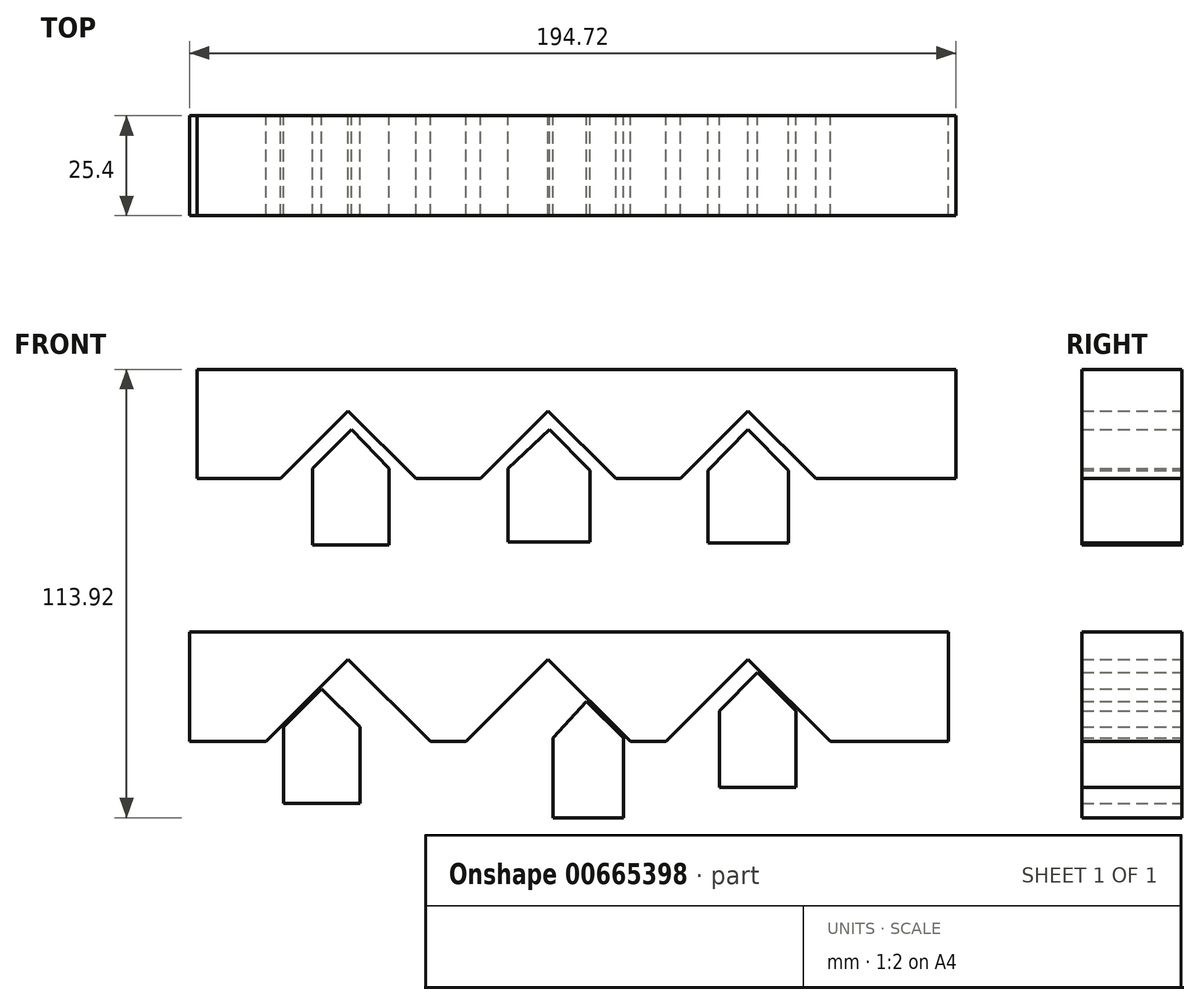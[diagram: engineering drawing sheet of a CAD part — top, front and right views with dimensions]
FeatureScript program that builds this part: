
annotation { "Feature Type Name" : "Feature", "Feature Type Description" : "" }
export const myFeature = defineFeature(function(context is Context, id is Id, definition is map)
    precondition{}
    {
        {
            var Q0;
            Q0=qCreatedBy(makeId("Front.planeOp"),FACE);
            var sketch = newSketch(context, id + "F0", { "sketchPlane" : qUnion([Q0])});
            skLineSegment(sketch, "E0", {"start": v(-96.29, 37.96) * mm, "end": v(96.47, 37.96) * mm});
            skLineSegment(sketch, "E1", {"start": v(96.47, 37.96) * mm, "end": v(96.47, 10.18) * mm});
            skLineSegment(sketch, "E2", {"start": v(96.47, 10.18) * mm, "end": v(60.84, 10.18) * mm});
            skLineSegment(sketch, "E3", {"start": v(60.84, 10.18) * mm, "end": v(43.68, 27.33) * mm});
            skLineSegment(sketch, "E4", {"start": v(43.68, 27.33) * mm, "end": v(26.53, 10.18) * mm});
            skLineSegment(sketch, "E5", {"start": v(26.53, 10.18) * mm, "end": v(10.04, 10.18) * mm});
            skLineSegment(sketch, "E6", {"start": v(-40.76, 10.18) * mm, "end": v(-57.92, 27.33) * mm});
            skLineSegment(sketch, "E7", {"start": v(-57.92, 27.33) * mm, "end": v(-75.07, 10.18) * mm});
            skLineSegment(sketch, "E8", {"start": v(-75.07, 10.18) * mm, "end": v(-96.29, 10.18) * mm});
            skLineSegment(sketch, "E9", {"start": v(-96.29, 10.18) * mm, "end": v(-96.29, 37.96) * mm});
            skLineSegment(sketch, "E10", {"start": v(-24.27, 10.18) * mm, "end": v(-7.12, 27.33) * mm});
            skLineSegment(sketch, "E11", {"start": v(-7.12, 27.33) * mm, "end": v(10.04, 10.18) * mm});
            skLineSegment(sketch, "E12.trimOffspring", {"start": v(-24.27, 10.18) * mm, "end": v(-40.76, 10.18) * mm});
            skLineSegment(sketch, "E13", {"start": v(-98.25, -28.81) * mm, "end": v(94.5, -28.81) * mm});
            skLineSegment(sketch, "E14", {"start": v(94.5, -28.81) * mm, "end": v(94.5, -56.6) * mm});
            skLineSegment(sketch, "E15", {"start": v(94.5, -56.6) * mm, "end": v(64.52, -56.6) * mm});
            skLineSegment(sketch, "E16", {"start": v(64.52, -56.6) * mm, "end": v(43.68, -35.77) * mm});
            skLineSegment(sketch, "E17", {"start": v(43.68, -35.77) * mm, "end": v(22.85, -56.6) * mm});
            skLineSegment(sketch, "E18", {"start": v(22.85, -56.6) * mm, "end": v(13.72, -56.6) * mm});
            skLineSegment(sketch, "E19", {"start": v(-37.08, -56.6) * mm, "end": v(-57.92, -35.77) * mm});
            skLineSegment(sketch, "E20", {"start": v(-57.92, -35.77) * mm, "end": v(-78.75, -56.6) * mm});
            skLineSegment(sketch, "E21", {"start": v(-78.75, -56.6) * mm, "end": v(-98.25, -56.6) * mm});
            skLineSegment(sketch, "E22", {"start": v(-98.25, -56.6) * mm, "end": v(-98.25, -28.81) * mm});
            skLineSegment(sketch, "E23", {"start": v(-27.95, -56.6) * mm, "end": v(-7.12, -35.77) * mm});
            skLineSegment(sketch, "E24", {"start": v(-7.12, -35.77) * mm, "end": v(13.72, -56.6) * mm});
            skLineSegment(sketch, "E25.trimOffspring", {"start": v(-27.95, -56.6) * mm, "end": v(-37.08, -56.6) * mm});
            skLineSegment(sketch, "E26", {"start": v(-57.1, 22.65) * mm, "end": v(-67.01, 12.74) * mm});
            skLineSegment(sketch, "E27", {"start": v(-47.57, 12.75) * mm, "end": v(-57.1, 22.65) * mm});
            skLineSegment(sketch, "E28", {"start": v(-6.74, 22.65) * mm, "end": v(-17.34, 12.75) * mm});
            skLineSegment(sketch, "E29", {"start": v(3.47, 12.24) * mm, "end": v(-6.74, 22.65) * mm});
            skLineSegment(sketch, "E30", {"start": v(43.64, 22.65) * mm, "end": v(33.42, 12.24) * mm});
            skLineSegment(sketch, "E31", {"start": v(53.86, 12.24) * mm, "end": v(43.64, 22.65) * mm});
            skLineSegment(sketch, "E32", {"start": v(-64.67, -43.22) * mm, "end": v(-74.39, -52.94) * mm});
            skLineSegment(sketch, "E33", {"start": v(-54.96, -52.94) * mm, "end": v(-64.67, -43.22) * mm});
            skLineSegment(sketch, "E34", {"start": v(2.65, -46.42) * mm, "end": v(-5.92, -55.74) * mm});
            skLineSegment(sketch, "E35", {"start": v(11.97, -55.74) * mm, "end": v(2.65, -46.42) * mm});
            skLineSegment(sketch, "E36", {"start": v(46.05, -39.08) * mm, "end": v(36.33, -48.8) * mm});
            skLineSegment(sketch, "E37", {"start": v(55.76, -48.8) * mm, "end": v(46.05, -39.08) * mm});
            skLineSegment(sketch, "E38", {"start": v(-67.01, 12.74) * mm, "end": v(-67.01, -6.7) * mm});
            skLineSegment(sketch, "E39", {"start": v(-67.01, -6.7) * mm, "end": v(-47.57, -6.7) * mm});
            skLineSegment(sketch, "E40", {"start": v(-47.57, -6.7) * mm, "end": v(-47.57, 12.75) * mm});
            skLineSegment(sketch, "E41", {"start": v(-17.34, 12.75) * mm, "end": v(-17.34, -5.87) * mm});
            skLineSegment(sketch, "E42", {"start": v(-17.34, -5.87) * mm, "end": v(3.47, -5.87) * mm});
            skLineSegment(sketch, "E43", {"start": v(3.47, -5.87) * mm, "end": v(3.47, 12.24) * mm});
            skLineSegment(sketch, "E44", {"start": v(33.42, 12.24) * mm, "end": v(33.42, -6.19) * mm});
            skLineSegment(sketch, "E45", {"start": v(33.42, -6.19) * mm, "end": v(53.86, -6.19) * mm});
            skLineSegment(sketch, "E46", {"start": v(53.86, -6.19) * mm, "end": v(53.86, 12.24) * mm});
            skLineSegment(sketch, "E47", {"start": v(-74.39, -52.94) * mm, "end": v(-74.39, -72.37) * mm});
            skLineSegment(sketch, "E48", {"start": v(-74.39, -72.37) * mm, "end": v(-54.96, -72.37) * mm});
            skLineSegment(sketch, "E49", {"start": v(-54.96, -72.37) * mm, "end": v(-54.96, -52.94) * mm});
            skLineSegment(sketch, "E50", {"start": v(-5.92, -55.74) * mm, "end": v(-5.92, -75.96) * mm});
            skLineSegment(sketch, "E51", {"start": v(-5.92, -75.96) * mm, "end": v(11.97, -75.96) * mm});
            skLineSegment(sketch, "E52", {"start": v(11.97, -75.96) * mm, "end": v(11.97, -55.74) * mm});
            skLineSegment(sketch, "E53", {"start": v(36.33, -48.8) * mm, "end": v(36.33, -68.23) * mm});
            skLineSegment(sketch, "E54", {"start": v(36.33, -68.23) * mm, "end": v(55.76, -68.23) * mm});
            skLineSegment(sketch, "E55", {"start": v(55.76, -68.23) * mm, "end": v(55.76, -48.8) * mm});
            skSolve(sketch);
        }
        {
            var Q0;
            Q0 = qSketchRegion(id + "F0", true);
            extrude(context, id + "F1", {"entities" : qUnion([Q0]), "depth" : 25.4 * mm, "offsetDistance" : 25.4 * mm});
        }
    });
